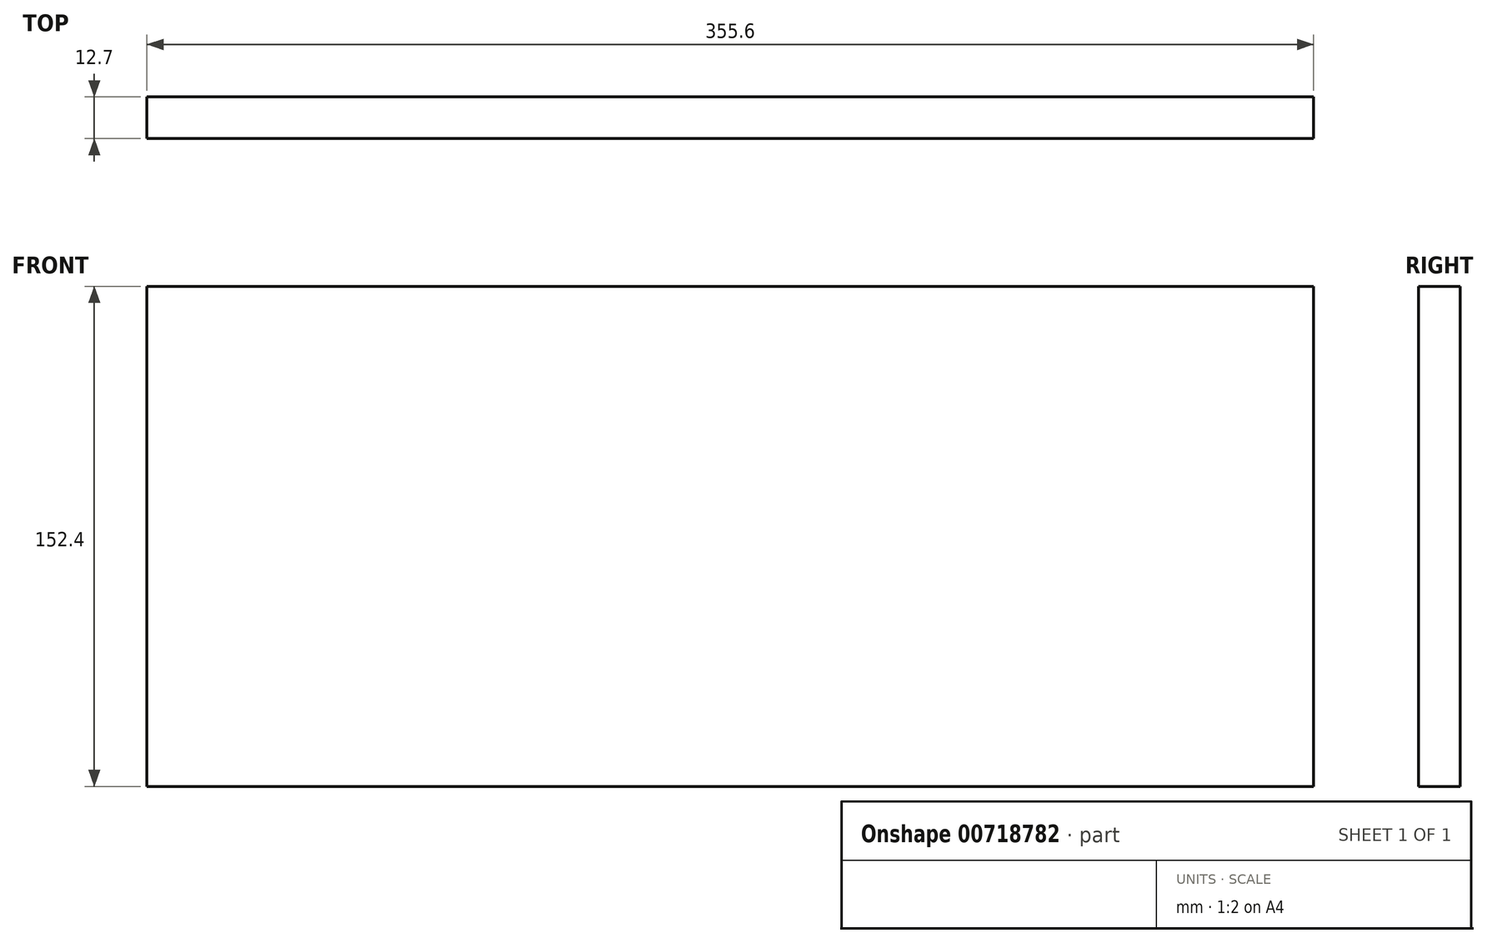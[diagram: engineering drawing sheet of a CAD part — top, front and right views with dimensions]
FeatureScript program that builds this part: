
annotation { "Feature Type Name" : "Feature", "Feature Type Description" : "" }
export const myFeature = defineFeature(function(context is Context, id is Id, definition is map)
    precondition{}
    {
        {
            var Q0;
            Q0=qCreatedBy(makeId("Front.planeOp"),FACE);
            var sketch = newSketch(context, id + "F0", { "sketchPlane" : qUnion([Q0])});
            skLineSegment(sketch, "E0.bottom", {"start": v(-159.69, 59.82) * mm, "end": v(195.91, 59.82) * mm});
            skLineSegment(sketch, "E0.top", {"start": v(-159.69, -92.58) * mm, "end": v(195.91, -92.58) * mm});
            skLineSegment(sketch, "E0.left", {"start": v(-159.69, 59.82) * mm, "end": v(-159.69, -92.58) * mm});
            skLineSegment(sketch, "E0.right", {"start": v(195.91, 59.82) * mm, "end": v(195.91, -92.58) * mm});
            skSolve(sketch);
        }
        {
            var Q0;
            Q0=makeQuery(id+"F0.imprint","IMPRINT",FACE,{"disambiguationData":[TD([[makeQuery(id+"F0.imprint","IMPRINT",EDGE,{"derivedFrom":sQuery(id+"F0.wireOp",EDGE,"E0.bottom")}),-1.0]])]});
            extrude(context, id + "F1", {"entities" : qUnion([Q0]), "depth" : 12.7 * mm, "offsetDistance" : 25.4 * mm});
        }
    });
